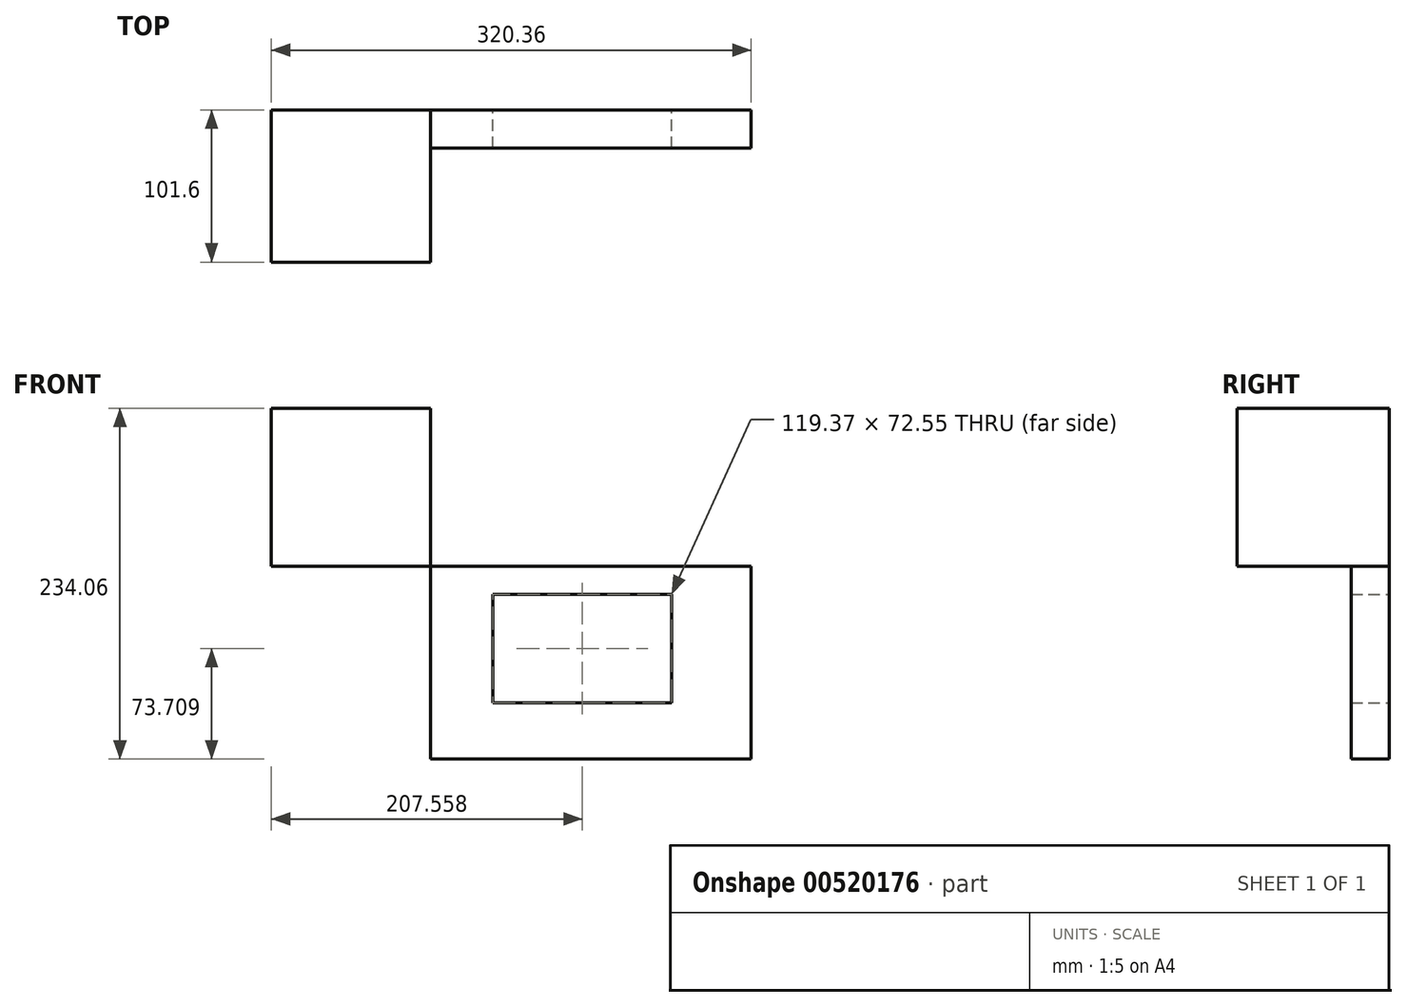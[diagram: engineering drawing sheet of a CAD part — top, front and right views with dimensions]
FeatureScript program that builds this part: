
annotation { "Feature Type Name" : "Feature", "Feature Type Description" : "" }
export const myFeature = defineFeature(function(context is Context, id is Id, definition is map)
    precondition{}
    {
        {
            var Q0;
            Q0=qCreatedBy(makeId("Front.planeOp"),FACE);
            var sketch = newSketch(context, id + "F0", { "sketchPlane" : qUnion([Q0])});
            skLineSegment(sketch, "E0.bottom", {"start": v(0, 0) * mm, "end": v(-106.18, 0) * mm});
            skLineSegment(sketch, "E0.top", {"start": v(0, 105.54) * mm, "end": v(-106.18, 105.54) * mm});
            skLineSegment(sketch, "E0.left", {"start": v(0, 0) * mm, "end": v(0, 105.54) * mm});
            skLineSegment(sketch, "E0.right", {"start": v(-106.18, 0) * mm, "end": v(-106.18, 105.54) * mm});
            skSolve(sketch);
        }
        {
            var Q0;
            Q0=makeQuery(id+"F0.imprint","IMPRINT",FACE,{"disambiguationData":[TD([[makeQuery(id+"F0.imprint","IMPRINT",EDGE,{"derivedFrom":sQuery(id+"F0.wireOp",EDGE,"E0.bottom")}),-1.0]])]});
            extrude(context, id + "F1", {"entities" : qUnion([Q0]), "depth" : 101.6 * mm, "offsetDistance" : 25.4 * mm});
        }
        {
            var Q0;
            Q0=qCreatedBy(makeId("Front.planeOp"),FACE);
            var sketch = newSketch(context, id + "F2", { "sketchPlane" : qUnion([Q0])});
            skLineSegment(sketch, "E1.bottom", {"start": v(0, 0) * mm, "end": v(214.18, 0) * mm});
            skLineSegment(sketch, "E1.top", {"start": v(0, -128.52) * mm, "end": v(214.18, -128.52) * mm});
            skLineSegment(sketch, "E1.left", {"start": v(0, 0) * mm, "end": v(0, -128.52) * mm});
            skLineSegment(sketch, "E1.right", {"start": v(214.18, 0) * mm, "end": v(214.18, -128.52) * mm});
            skLineSegment(sketch, "E2.bottom", {"start": v(41.7, -18.54) * mm, "end": v(161.06, -18.54) * mm});
            skLineSegment(sketch, "E2.top", {"start": v(41.7, -91.08) * mm, "end": v(161.06, -91.08) * mm});
            skLineSegment(sketch, "E2.left", {"start": v(41.7, -18.54) * mm, "end": v(41.7, -91.08) * mm});
            skLineSegment(sketch, "E2.right", {"start": v(161.06, -18.54) * mm, "end": v(161.06, -91.08) * mm});
            skLineSegment(sketch, "E3.bottom", {"start": v(161.06, -91.08) * mm, "end": v(41.7, -91.08) * mm});
            skLineSegment(sketch, "E3.top", {"start": v(161.06, -18.54) * mm, "end": v(41.7, -18.54) * mm});
            skLineSegment(sketch, "E3.left", {"start": v(161.06, -91.08) * mm, "end": v(161.06, -18.54) * mm});
            skLineSegment(sketch, "E3.right", {"start": v(41.7, -91.08) * mm, "end": v(41.7, -18.54) * mm});
            skSolve(sketch);
        }
        {
            var Q0;
            Q0=makeQuery(id+"F2.imprint","IMPRINT",FACE,{"disambiguationData":[TD([[makeQuery(id+"F2.imprint","IMPRINT",EDGE,{"derivedFrom":sQuery(id+"F2.wireOp",EDGE,"E1.bottom")}),-1.0]])]});
            extrude(context, id + "F3", {"entities" : qUnion([Q0]), "depth" : 25.4 * mm, "offsetDistance" : 25.4 * mm});
        }
    });
